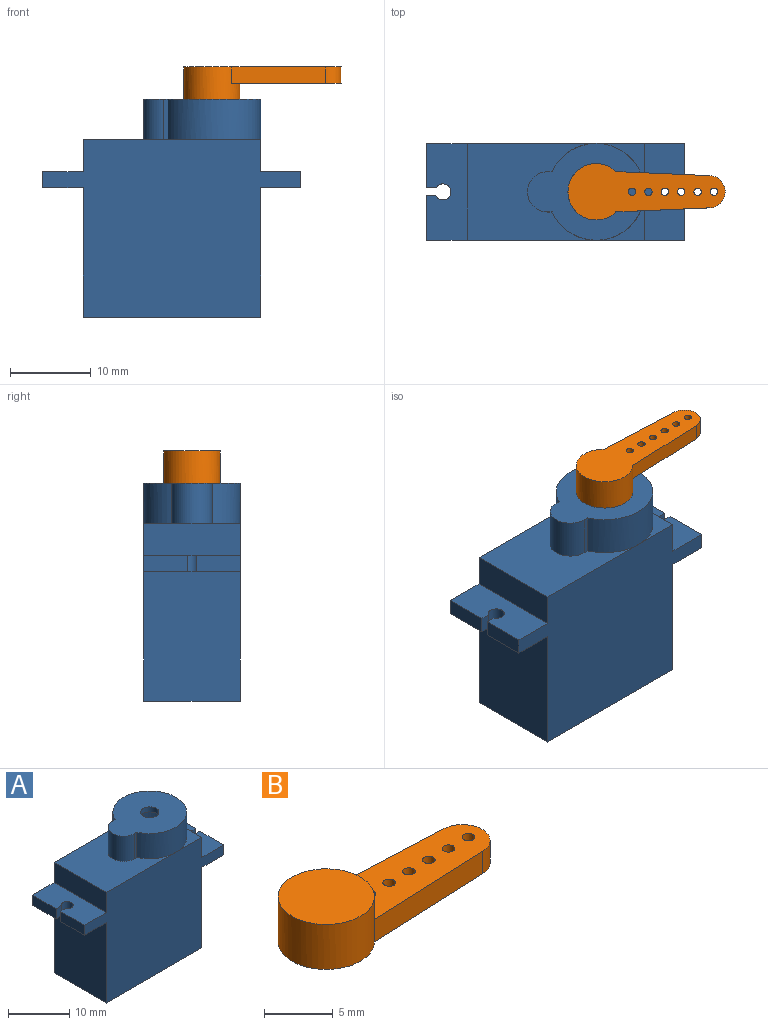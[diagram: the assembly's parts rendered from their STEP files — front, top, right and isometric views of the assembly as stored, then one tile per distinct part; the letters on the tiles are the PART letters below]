
ASSEMBLY  parts=2 mates=1
PART A: 43 faces, bbox 32x12x27 mm
  f0: plane 15x10mm, normal (0,0,-1), area 104mm2, adj f3,f4,f5,f8,f10,f11,f12
  f1: plane 5x5mm, normal (0,0,-1), area 5.4mm2, adj f2,f5,f8
  f2: plane 20x10mm, normal (-1,0,0), area 200mm2, adj f1,f4,f5,f6,f7
  f3: plane 20x10mm, normal (1,0,0), area 200mm2, adj f0,f4,f5,f7
  f4: plane 20x20mm, normal (0,-1,0), area 400mm2, adj f0,f2,f3,f6,f7
  f5: plane 20x20mm, normal (0,1,0), area 400mm2, adj f0,f1,f2,f3,f7
  f6: plane 5x5mm, normal (0,0,-1), area 5.4mm2, adj f2,f4,f8
  f7: plane 20x10mm, normal (0,0,1), area 200mm2, adj f2,f3,f4,f5
  f8: cylinder r=5mm len=10mm, axis (0,0,-1), area 141.8mm2, adj f0,f1,f6,f9,f11,f12
  f9: plane 12.5x10mm, normal (0,0,-1), area 78.2mm2, adj f8,f10,f11,f12,f13
  f10: cylinder r=1.5mm len=5mm, axis (0,0,-1), area 23.6mm2, adj f0,f9,f11,f12
  f11: plane 5x1.23mm, normal (0,1,0), area 6.2mm2, adj f0,f8,f9,f10
  f12: plane 5x1.23mm, normal (0,-1,0), area 6.2mm2, adj f0,f8,f9,f10
  f13: cylinder r=1.5mm len=3mm, axis (0,0,1), area 9.4mm2, adj f9,f39
  f14: plane 16x12mm, normal (0,0,1), area 124.7mm2, adj f25,f26,f27,f38,f40,f41,f42
  f15: plane 6x6mm, normal (0,0,1), area 7.7mm2, adj f22,f27,f38
  f16: plane 12x5mm, normal (0,0,1), area 55.8mm2, adj f18,f25,f26,f27,f30,f35,f36,f37
  f17: plane 12x5mm, normal (0,0,-1), area 55.8mm2, adj f18,f24,f26,f27,f30,f35,f36,f37
  f18: plane 5.5x2mm, normal (-1,0,0), area 11mm2, adj f16,f17,f26,f36
  f19: plane 12x5mm, normal (0,0,-1), area 55.8mm2, adj f21,f23,f26,f27,f31,f32,f33,f34
  f20: plane 12x5mm, normal (0,0,1), area 55.8mm2, adj f21,f22,f26,f27,f31,f32,f33,f34
  f21: plane 5.5x2mm, normal (1,0,0), area 11mm2, adj f19,f20,f27,f33
  f22: plane 12x4mm, normal (1,0,0), area 48mm2, adj f15,f20,f26,f27,f28
  f23: plane 16x12mm, normal (1,0,0), area 192mm2, adj f19,f26,f27,f29
  f24: plane 16x12mm, normal (-1,0,0), area 192mm2, adj f17,f26,f27,f29
  f25: plane 12x4mm, normal (-1,0,0), area 48mm2, adj f14,f16,f26,f27
  f26: plane 32x22mm, normal (0,1,0), area 504mm2, adj f14,f16,f17,f18,f19,f20,f22,f23
  f27: plane 32x22mm, normal (0,-1,0), area 504mm2, adj f14,f15,f16,f17,f19,f20,f21,f22
  f28: plane 6x6mm, normal (0,0,1), area 7.7mm2, adj f22,f26,f38
  f29: plane 22x12mm, normal (0,0,-1), area 264mm2, adj f23,f24,f26,f27
  f30: plane 5.5x2mm, normal (-1,0,0), area 11mm2, adj f16,f17,f27,f37
  f31: plane 5.5x2mm, normal (1,0,0), area 11mm2, adj f19,f20,f26,f34
  f32: cylinder r=1mm len=2mm, axis (0,0,1), area 10.5mm2, adj f19,f20,f33,f34
  f33: plane 2x1.13mm, normal (0,1,0), area 2.3mm2, adj f19,f20,f21,f32
  f34: plane 2x1.13mm, normal (0,-1,0), area 2.3mm2, adj f19,f20,f31,f32
  f35: cylinder r=1mm len=2mm, axis (0,0,1), area 10.5mm2, adj f16,f17,f36,f37
  f36: plane 2x1.13mm, normal (0,-1,0), area 2.3mm2, adj f16,f17,f18,f35
  f37: plane 2x1.13mm, normal (0,1,0), area 2.3mm2, adj f16,f17,f30,f35
  f38: cylinder r=6mm len=12mm, axis (0,0,-1), area 162.7mm2, adj f14,f15,f28,f39,f41,f42
  f39: plane 14.5x12mm, normal (0,0,1), area 116.7mm2, adj f13,f38,f40,f41,f42
  f40: cylinder r=2.5mm len=5mm, axis (0,0,-1), area 39.3mm2, adj f14,f39,f41,f42
  f41: plane 5x0.55mm, normal (0,-1,0), area 2.7mm2, adj f14,f38,f39,f40
  f42: plane 5x0.55mm, normal (0,1,0), area 2.7mm2, adj f14,f38,f39,f40
PART B: 13 faces, bbox 19.5x7x4 mm
  f0: cylinder r=3.5mm len=7mm, axis (0,0,-1), area 76.8mm2, adj f1,f2,f3,f4,f6
  f1: plane 7x7mm, normal (0,0,1), area 38.5mm2, adj f0
  f2: plane 19.5x7mm, normal (0,0,-1), area 89.2mm2, adj f0,f3,f4,f5,f7,f8,f9,f10
  f3: plane 11.64x2mm, normal (0.04,-1,0), area 23.3mm2, adj f0,f2,f5,f6
  f4: plane 11.64x2mm, normal (0.04,1,0), area 23.3mm2, adj f0,f2,f5,f6
  f5: cylinder r=2mm len=4mm, axis (0,0,-1), area 12.2mm2, adj f2,f3,f4,f6
  f6: plane 13.55x5mm, normal (0,0,1), area 50.7mm2, adj f0,f3,f4,f5,f7,f8,f9,f10
  f7: cylinder r=0.46mm len=2mm, axis (0,0,1), area 5.7mm2, adj f2,f6
  f8: cylinder r=0.46mm len=2mm, axis (0,0,1), area 5.7mm2, adj f2,f6
  f9: cylinder r=0.46mm len=2mm, axis (0,0,1), area 5.7mm2, adj f2,f6
  f10: cylinder r=0.46mm len=2mm, axis (0,0,1), area 5.7mm2, adj f2,f6
  f11: cylinder r=0.46mm len=2mm, axis (0,0,1), area 5.7mm2, adj f2,f6
  f12: cylinder r=0.46mm len=2mm, axis (0,0,1), area 5.7mm2, adj f2,f6
PLACE A t=(-14.66,-7.81,6.01)mm
PLACE B rot(axis=(1,0,0),180deg) t=(-20.66,-1.81,37.01)mm
MATE revolute B.f0 <-> A.f8  axis (0,0,-1) through (-20.66,-1.81,33.01)mm
